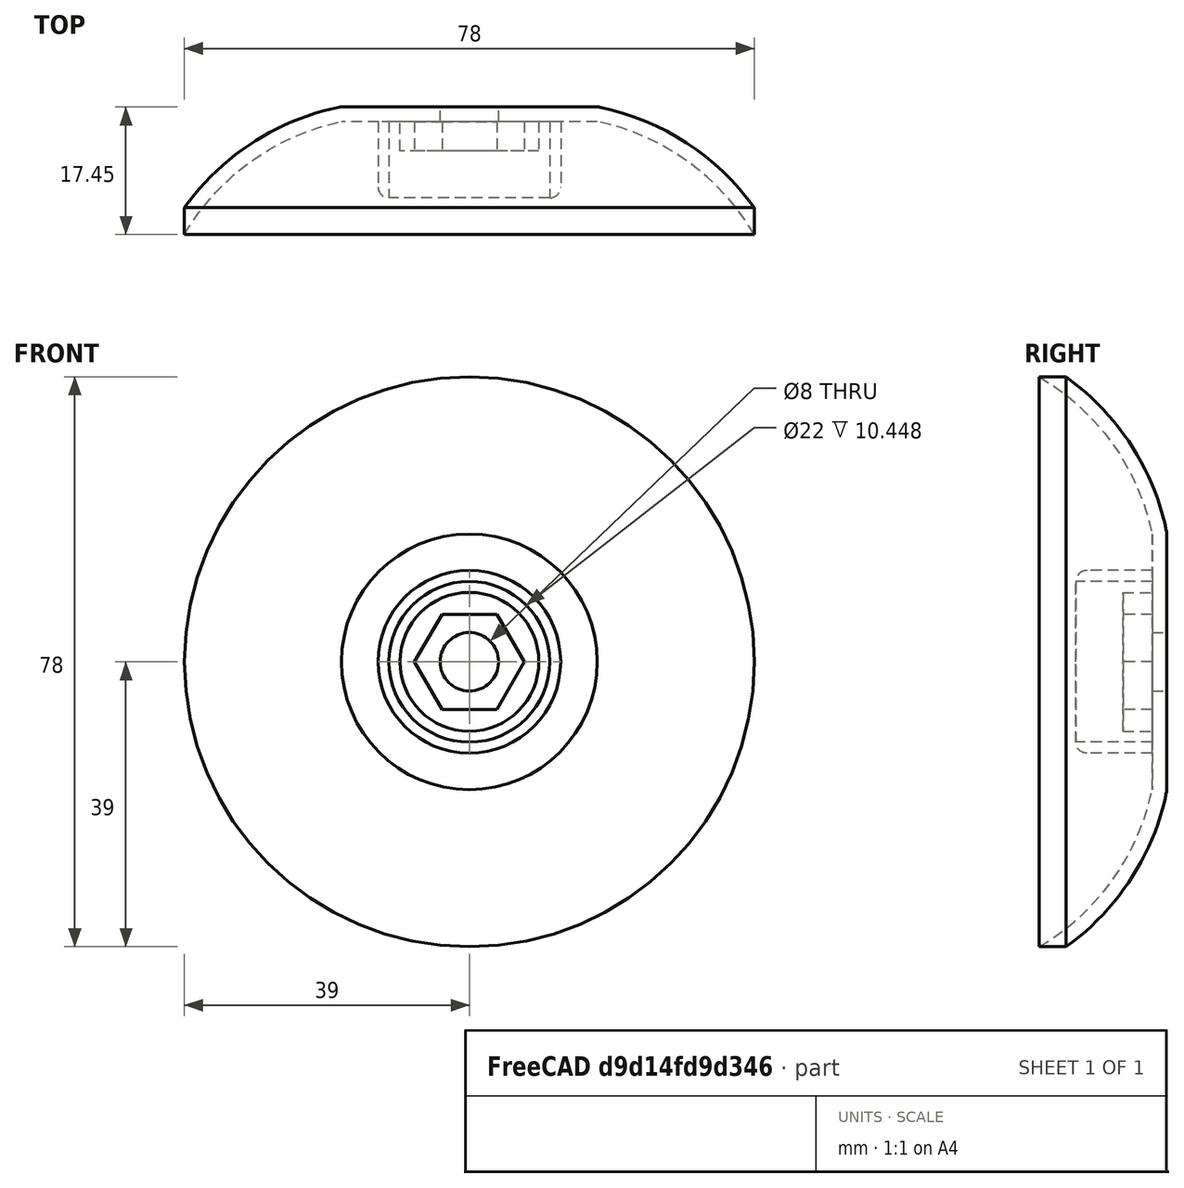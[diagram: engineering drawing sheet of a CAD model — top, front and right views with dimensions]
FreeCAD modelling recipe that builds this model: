
FCSTD DOCUMENT  (FreeCAD 0.18.4R)
Label: 14
License: All rights reserved
LicenseURL: http://en.wikipedia.org/wiki/All_rights_reserved
objects: Sketcher::SketchObject×2, PartDesign::Revolution×1, PartDesign::Pad×1, PartDesign::Body×1
note: 7 computed .brp shape members not serialized (recipe doc carries the construction recipe); baked Part::Feature solids carry a one-line shape summary decoded from their .brp

FEATURE [Sketcher::SketchObject] Sketch
  MapMode = 5
  Support = -> [XY_Plane]
  constraints (46):
    c: Horizontal(g0)
    c: PointOnObject(g1,g-1)
    c: Coincident(g1,g0)
    c: PointOnObject(g1,g-1)
    c: Distance(g1,g-2) = 43.5
    c: Coincident(g2,g0)
    c: PointOnObject(g3,g-1)
    c: PointOnObject(g3,g-1)
    c: Coincident(g4,g1)
    c: Coincident(g4,g3)
    c: Distance(g4) = 2
    c: Distance(g2) = 2
    c: Coincident(g5,g0)
    c: Coincident(g5,g3)
    c: Coincident(g6,g2)
    c: Coincident(g6,g5)
    c: Horizontal(g6)
    c: Tangent(g6,g5)
    c: Tangent(g5,g3)
    c: Vertical(g2)
    c: DistanceY(g-1,g0) = 32
    c: Distance(g0,g-2) = 17.5
    c: Distance(g0,g-2) = 4
    c: Coincident(g7,g1)
    c: Coincident(g7,g0)
    c: Coincident(g8,g7)
    c: Coincident(g8,g5)
    c: Coincident(g9,g7)
    c: Coincident(g9,g8)
    c: Vertical(g9)
    c: Distance(g7,g-2) = 39
    c: Coincident(g10,g5)
    c: PointOnObject(g10,g0)
    c: Distance(g10) = 5
    c: Coincident(g11,g10)
    c: Vertical(g11)
    c: PointOnObject(g12,g0)
    c: Vertical(g12)
    c: Coincident(g13,g11)
    c: Coincident(g13,g12)
    c: PointOnObject(g13,g12)
    c: Tangent(g13,g11)
    c: DistanceY(g7,g12) = 5
    c: Coincident(g14,g2)
    c: Coincident(g14,g12)
    c: Distance(g14) = 7
FEATURE [PartDesign::Revolution] Revolution
  Angle = 360
  Axis = (0,1,0)
  Base = (0,0,0)
  Profile = -> Sketch
  ReferenceAxis = -> Sketch [V_Axis]
  Reversed = true
FEATURE [Sketcher::SketchObject] Sketch001  label="Unnamed"
  constraints (21):
    c: Coincident(g0,g1)
    c: Coincident(g1,g2)
    c: Coincident(g2,g3)
    c: Coincident(g3,g4)
    c: Coincident(g4,g5)
    c: Coincident(g5,g0)
    c: Equal(g0, g1-g5) x5
    c: PointOnObject(g0,g6)
    c: PointOnObject(g1,g6)
    c: PointOnObject(g2,g6)
    c: PointOnObject(g3,g6)
    c: PointOnObject(g4,g6)
    c: PointOnObject(g5,g6)
    c: Coincident(g6,g-1)
    c: Distance(g3,g0) = 13
    c: Horizontal(g0)
    c: Coincident(g7,g-1)
    c: Coincident(g8,g4)
    c: PointOnObject(g8,g7)
    c: Horizontal(g8)
    c: Distance(g8) = 2
FEATURE [PartDesign::Pad] Pad  label="Unnamed"
  Length = 100
  Length2 = 100
  Type = 0
FEATURE [PartDesign::Body] Body
  Group = -> [Sketch,Revolution,Sketch001,Pad]
  Origin = -> Origin
  Tip = -> Pad
